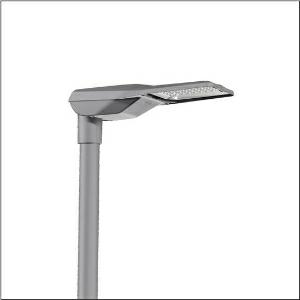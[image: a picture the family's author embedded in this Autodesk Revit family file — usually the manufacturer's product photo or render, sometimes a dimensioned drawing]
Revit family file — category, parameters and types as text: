
# Revit family: streetlight_sl_21_iq_mini___stw1_0a_5xe2e41g08gb_cbe1
name_source: partatom
category: Lighting Fixtures
units: mm (PartAtom-declared; Revit-internal decimal feet)

## family parameters
Cut with Voids When Loaded = No
Host = Face
Light Source = No
Part Type = Normal
Room Calculation Point = No
Round Connector Dimension = Use Diameter
Shared = No

## types (1)
- --- (1 x LED, 5920 lm, 37.1 W, 4000K)
    Apparent Load = 37 VA
    CIE Flux Codes = 38 75 98 100 100
    Color Rendering = 70
    Color Temperature = 4000K
    Default Elevation = 1800 mm
    Description = Streetlight SL 21 iQ mini, mast luminaire, primary light control with lens, of PMMA, primary optical cover: cover, of toughened safety glass, transparent, light distribution: STW1.0a, light emission: direct distribution, primary light characteristic: asymmetric, installation type: post-top, side-entry, LED, High Power LED, rated luminous flux: 5.920lm, luminous efficacy: 160lm/W, light colour: 740, colour temperature: 4000K, control gear: iQ Street-Remote, control: Street-Remote, Auto-Match, Temp-Guard, Lumen-Switch, Night-Set, Smart-Wire, Light-Fading, Desk-Remote (wireless, voltage-free reading and setting of iQ features in the workshop via application-optimized NFC function/RFID function), optimised constant luminous flux control (CLO 2.0), pre-setting: linear dimming characteristic, mains connection: 220..240V, AC, 50/60Hz, start of lifetime: 37W, end of service life: 39W, reduction: 18W, luminaire housing, of diecast aluminium, powder-coated, Siteco® metallic grey (DB 702S), corrosivity category C5 mid according to DIN EN ISO 12944, please order mast flange separately, inclination adjustable: 0°, 5°, 10°, 15°, sealing non-destructively replaceable, multi-level sealing system, length: 628mm, width: 235mm, height: 110mm, mast flange for spigot size: 42mm (side-entry): 5XC10008XM4, 60/48mm (side-entry/post-top): 5XC10108XM2, 76/60mm (side-entry/post-top): 5XC10108XM1, mounting height: 4..8m, protection rating (complete): IP66, insulation class (complete): insulation class II (safety insulation), certification: CE, ENEC, ENEC+, VDE, impact resistance: IK10, permissible operating ambient temperature for outdoor applications: -40..+50°C, standard-compliant lighting for roads and squares, packaging unit: 1 piece

Light Distribution: STW1.0a
    Height = 110 mm
    Lamp = 1 x LED
    Lamp Light Flux = 5920 lm
    Lamp Power = 37.1 W
    Lamp count = 1
    Length = 625 mm
    Luminous efficacy = 160 lm/W
    Manufacturer = Siteco
    ModVariant = No
    Model = 5XE2E41G08GB
    Number of Poles = 1
    OnlyDefault = Yes
    Power Factor = 1
    Product Name = Streetlight SL 21 iQ mini | STW1.0a
    Product group = mast luminaire | pylon top
    ProductGroupID = 6100
    Protection Class = Protection class II
    Protection Degree = IP 66
    RLX_Detail_Level = 1
    RLX_Emergency_Light_Flux = 0 lm
    RLX_Emergency_Type = 0
    RLX_Emergency_Type_DB = No
    RlxData = <blob elided: 26389 chars, md5=a9f279b5>
    Socket = socket
    Standby Power = 0 W
    System Light Flux = 5920 lm
    System Power = 37 W
    Type Comments = factory setting: luminous flux: 100 % | dim-lin: 254 | 385 mA
    Type Image = l_1003519.jpg
    URL = http://relux.com
    VarID = @adj_187482
    Voltage = 0 V
    Weight = 0.00 kg
    Width = 234 mm

## geometry (parser evidence)
native form markers: Blend x4, Sweep x11
no freeform markers — native parametric forms only
